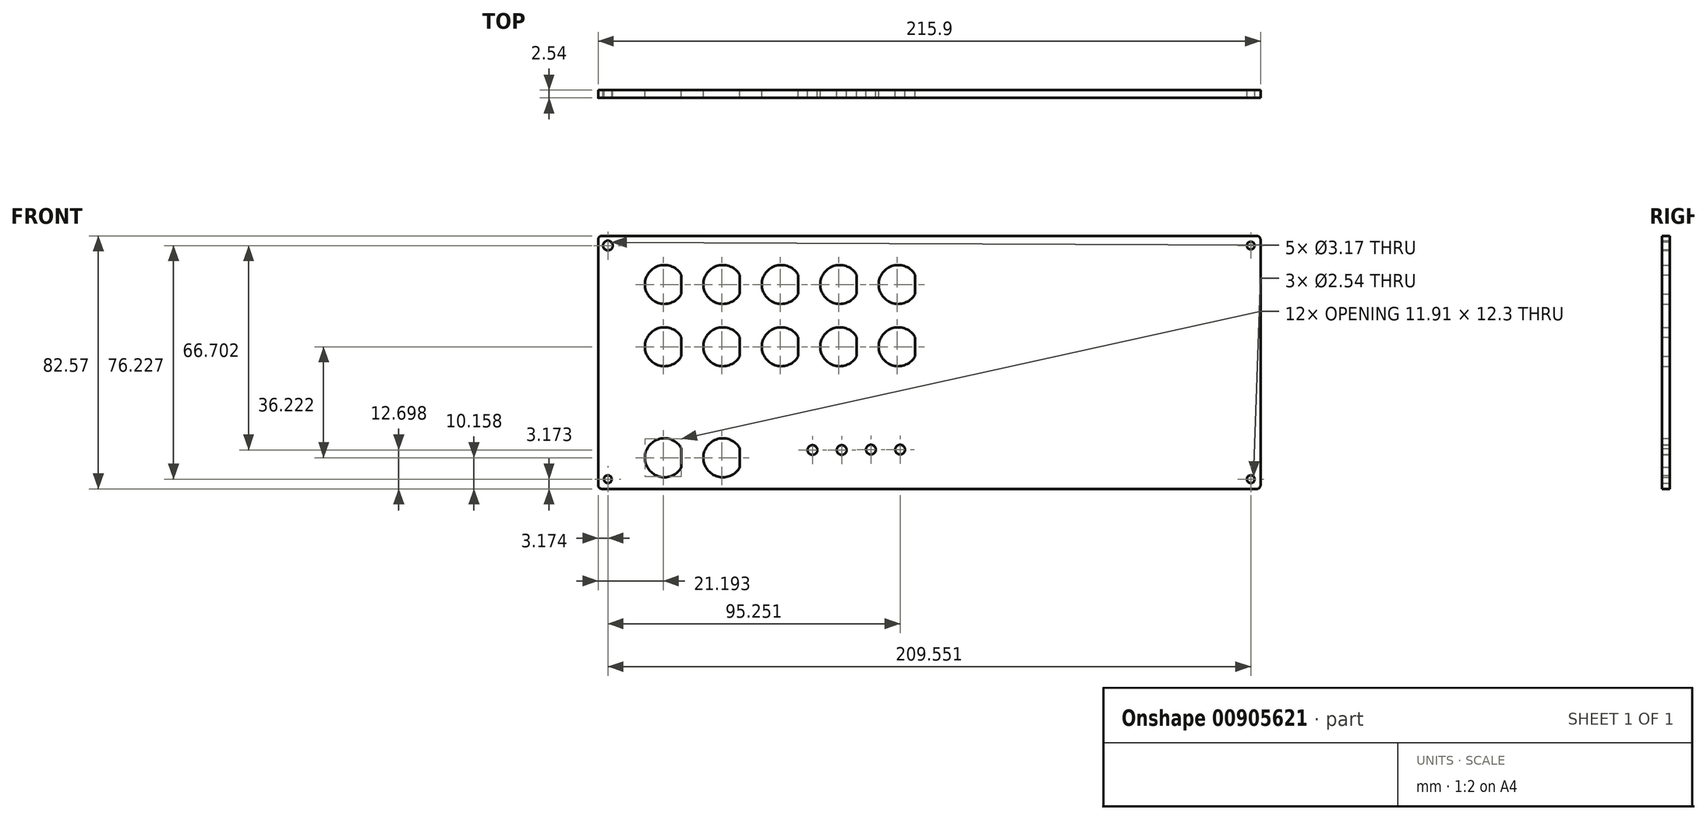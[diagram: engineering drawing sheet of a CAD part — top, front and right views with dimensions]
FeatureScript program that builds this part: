
annotation { "Feature Type Name" : "Feature", "Feature Type Description" : "" }
export const myFeature = defineFeature(function(context is Context, id is Id, definition is map)
    precondition{}
    {
        {
            var Q0;
            Q0=qCreatedBy(makeId("Front.planeOp"),FACE);
            var sketch = newSketch(context, id + "F0", { "sketchPlane" : qUnion([Q0])});
            skLineSegment(sketch, "E0.bottom", {"start": v(-106.68, 41.27) * mm, "end": v(106.68, 41.28) * mm});
            skLineSegment(sketch, "E0.top", {"start": v(-106.68, -41.3) * mm, "end": v(106.68, -41.3) * mm});
            skLineSegment(sketch, "E0.left", {"start": v(-107.95, 40) * mm, "end": v(-107.95, -40.03) * mm});
            skLineSegment(sketch, "E0.right", {"start": v(107.95, 40) * mm, "end": v(107.95, -40.03) * mm});
            skArc(sketch, "E1", {"start": v(-80.8, 28.47) * mm, "mid": v(-92.71, 25.4) * mm, "end": v(-80.8, 22.33) * mm});
            skPoint(sketch, "E2.start.orphan", {"position": v(-92.7, 25.4) * mm});
            skLineSegment(sketch, "E3", {"start": v(-80.8, 22.33) * mm, "end": v(-80.8, 28.47) * mm});
            skArc(sketch, "E4", {"start": v(-61.75, 28.47) * mm, "mid": v(-73.66, 25.4) * mm, "end": v(-61.75, 22.33) * mm});
            skPoint(sketch, "E5.start.orphan", {"position": v(-73.66, 25.4) * mm});
            skLineSegment(sketch, "E6", {"start": v(-61.75, 22.33) * mm, "end": v(-61.75, 28.47) * mm});
            skArc(sketch, "E7", {"start": v(-42.7, 28.47) * mm, "mid": v(-54.61, 25.4) * mm, "end": v(-42.7, 22.33) * mm});
            skPoint(sketch, "E8.start.orphan", {"position": v(-54.61, 25.4) * mm});
            skLineSegment(sketch, "E9", {"start": v(-42.7, 22.33) * mm, "end": v(-42.7, 28.47) * mm});
            skArc(sketch, "E10", {"start": v(-23.65, 28.47) * mm, "mid": v(-35.56, 25.4) * mm, "end": v(-23.65, 22.33) * mm});
            skPoint(sketch, "E11.start.orphan", {"position": v(-35.56, 25.4) * mm});
            skLineSegment(sketch, "E12", {"start": v(-23.65, 22.33) * mm, "end": v(-23.65, 28.47) * mm});
            skArc(sketch, "E13", {"start": v(-4.6, 28.47) * mm, "mid": v(-16.51, 25.4) * mm, "end": v(-4.6, 22.33) * mm});
            skPoint(sketch, "E14.start.orphan", {"position": v(-16.51, 25.4) * mm});
            skLineSegment(sketch, "E15", {"start": v(-4.6, 22.33) * mm, "end": v(-4.6, 28.47) * mm});
            skArc(sketch, "E16", {"start": v(-80.8, 8.15) * mm, "mid": v(-92.7, 5.08) * mm, "end": v(-80.8, 2) * mm});
            skPoint(sketch, "E17.start.orphan", {"position": v(-92.7, 5.08) * mm});
            skLineSegment(sketch, "E18", {"start": v(-80.8, 2) * mm, "end": v(-80.8, 8.15) * mm});
            skArc(sketch, "E19", {"start": v(-61.75, 8.15) * mm, "mid": v(-73.66, 5.08) * mm, "end": v(-61.75, 2) * mm});
            skPoint(sketch, "E20.start.orphan", {"position": v(-73.66, 5.08) * mm});
            skLineSegment(sketch, "E21", {"start": v(-61.75, 2) * mm, "end": v(-61.75, 8.15) * mm});
            skArc(sketch, "E22", {"start": v(-42.7, 8.15) * mm, "mid": v(-54.61, 5.08) * mm, "end": v(-42.7, 2) * mm});
            skPoint(sketch, "E23.start.orphan", {"position": v(-54.61, 5.08) * mm});
            skLineSegment(sketch, "E24", {"start": v(-42.7, 2) * mm, "end": v(-42.7, 8.15) * mm});
            skArc(sketch, "E25", {"start": v(-23.65, 8.15) * mm, "mid": v(-35.56, 5.08) * mm, "end": v(-23.65, 2) * mm});
            skPoint(sketch, "E26.start.orphan", {"position": v(-35.56, 5.08) * mm});
            skLineSegment(sketch, "E27", {"start": v(-23.65, 2) * mm, "end": v(-23.65, 8.15) * mm});
            skArc(sketch, "E28", {"start": v(-4.6, 8.15) * mm, "mid": v(-16.51, 5.08) * mm, "end": v(-4.6, 2) * mm});
            skPoint(sketch, "E29.start.orphan", {"position": v(-16.51, 5.08) * mm});
            skLineSegment(sketch, "E30", {"start": v(-4.6, 2) * mm, "end": v(-4.6, 8.15) * mm});
            skArc(sketch, "E31", {"start": v(-80.8, -28.07) * mm, "mid": v(-92.7, -31.14) * mm, "end": v(-80.8, -34.22) * mm});
            skPoint(sketch, "E32.start.orphan", {"position": v(-92.7, -31.14) * mm});
            skLineSegment(sketch, "E33", {"start": v(-80.8, -34.22) * mm, "end": v(-80.8, -28.07) * mm});
            skArc(sketch, "E34", {"start": v(-61.75, -28.07) * mm, "mid": v(-73.66, -31.14) * mm, "end": v(-61.75, -34.22) * mm});
            skPoint(sketch, "E35.start.orphan", {"position": v(-73.66, -31.14) * mm});
            skLineSegment(sketch, "E36", {"start": v(-61.75, -34.22) * mm, "end": v(-61.75, -28.07) * mm});
            skCircle(sketch, "E37", {"center": v(-38.1, -28.6) * mm, "radius": 1.59 * mm});
            skCircle(sketch, "E38", {"center": v(-28.58, -28.6) * mm, "radius": 1.59 * mm});
            skCircle(sketch, "E39", {"center": v(-19.05, -28.47) * mm, "radius": 1.59 * mm});
            skCircle(sketch, "E40", {"center": v(-9.53, -28.47) * mm, "radius": 1.59 * mm});
            skArc(sketch, "E41", {"start": v(-106.68, 41.28) * mm, "mid": v(-107.58, 40.9) * mm, "end": v(-107.95, 40) * mm});
            skArc(sketch, "E42", {"start": v(-107.95, -40.03) * mm, "mid": v(-107.58, -40.93) * mm, "end": v(-106.68, -41.3) * mm});
            skArc(sketch, "E43", {"start": v(106.68, -41.3) * mm, "mid": v(107.58, -40.93) * mm, "end": v(107.95, -40.03) * mm});
            skArc(sketch, "E44", {"start": v(107.95, 40) * mm, "mid": v(107.58, 40.9) * mm, "end": v(106.68, 41.28) * mm});
            skCircle(sketch, "E45", {"center": v(104.78, 38.1) * mm, "radius": 1.27 * mm});
            skCircle(sketch, "E46", {"center": v(104.78, -38.13) * mm, "radius": 1.27 * mm});
            skCircle(sketch, "E47", {"center": v(-104.78, 38.1) * mm, "radius": 1.59 * mm});
            skCircle(sketch, "E48", {"center": v(-104.78, -38.13) * mm, "radius": 1.27 * mm});
            skSolve(sketch);
        }
        {
            var Q0;
            Q0=makeQuery(id+"F0.imprint","IMPRINT",FACE,{"disambiguationData":[TD([[makeQuery(id+"F0.imprint","IMPRINT",EDGE,{"derivedFrom":sQuery(id+"F0.wireOp",EDGE,"E0.bottom")}),-1.0]])]});
            extrude(context, id + "F1", {"entities" : qUnion([Q0]), "depth" : 2.54 * mm, "offsetDistance" : 25.4 * mm});
        }
    });
